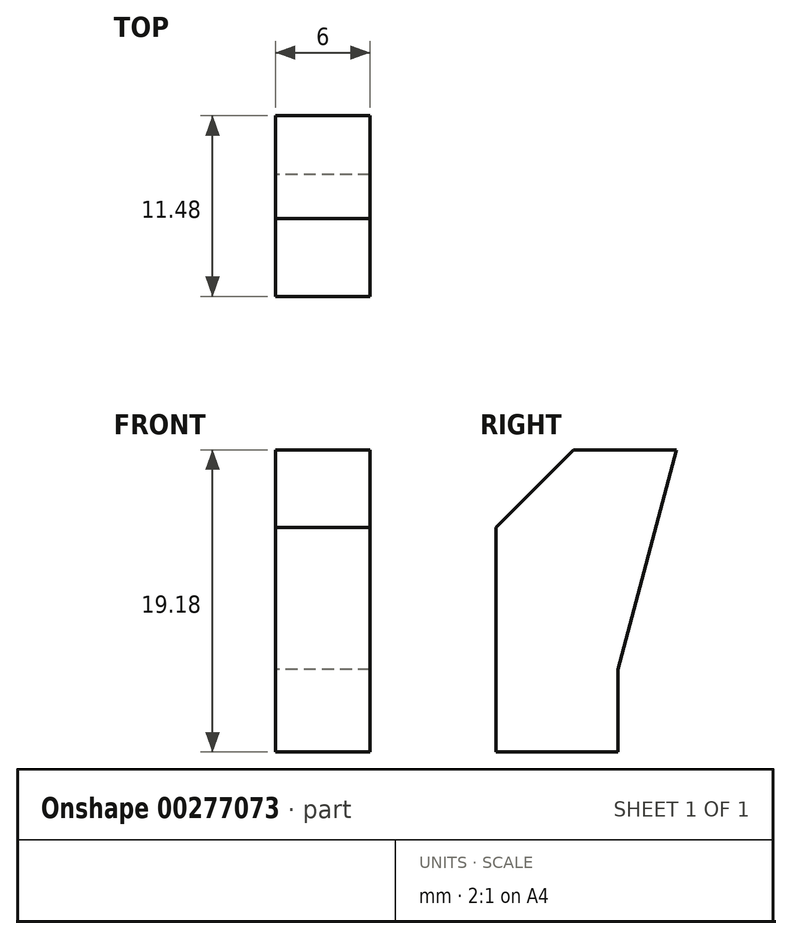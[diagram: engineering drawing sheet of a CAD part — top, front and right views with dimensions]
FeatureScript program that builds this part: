
annotation { "Feature Type Name" : "Feature", "Feature Type Description" : "" }
export const myFeature = defineFeature(function(context is Context, id is Id, definition is map)
    precondition{}
    {
        {
            var Q0;
            Q0=qCreatedBy(makeId("Right.planeOp"),FACE);
            var sketch = newSketch(context, id + "F0", { "sketchPlane" : qUnion([Q0])});
            skLineSegment(sketch, "E0", {"start": v(0, 0) * mm, "end": v(-6.99, 0) * mm, "construction": true});
            skLineSegment(sketch, "E1", {"start": v(-6.99, 0) * mm, "end": v(-12.06, -5.08) * mm, "construction": true});
            skLineSegment(sketch, "E2", {"start": v(-12.07, -5.08) * mm, "end": v(-12.06, -19.68) * mm, "construction": true});
            skLineSegment(sketch, "E3", {"start": v(-12.07, -19.69) * mm, "end": v(-3.8, -19.69) * mm, "construction": true});
            skLineSegment(sketch, "E4", {"start": v(-3.8, -19.69) * mm, "end": v(-3.8, -14.22) * mm, "construction": true});
            skLineSegment(sketch, "E5", {"start": v(-3.8, -14.22) * mm, "end": v(0, 0) * mm, "construction": true});
            skLineSegment(sketch, "E6.0", {"start": v(-11.81, -5.19) * mm, "end": v(-11.81, -19.43) * mm});
            skLineSegment(sketch, "E6.1", {"start": v(-6.88, -0.25) * mm, "end": v(-11.81, -5.19) * mm});
            skLineSegment(sketch, "E6.2", {"start": v(0, -0.25) * mm, "end": v(-0.07, -0.25) * mm, "construction": true});
            skLineSegment(sketch, "E7.0", {"start": v(-4.06, -14.19) * mm, "end": v(-0.33, -0.25) * mm});
            skLineSegment(sketch, "E7.1", {"start": v(-11.81, -19.43) * mm, "end": v(-4.06, -19.43) * mm});
            skLineSegment(sketch, "E8.0", {"start": v(-4.06, -19.43) * mm, "end": v(-4.06, -14.19) * mm});
            skLineSegment(sketch, "E9.trimOffspring", {"start": v(-0.33, -0.25) * mm, "end": v(-6.88, -0.25) * mm});
            skSolve(sketch);
        }
        {
            var Q0;
            Q0 = qSketchRegion(id + "F0", true);
            extrude(context, id + "F1", {"entities" : qUnion([Q0]), "endBound" : BoundingType.SYMMETRIC, "depth" : (6.2 - 2 * (.1)) * mm, "offsetDistance" : 25.4 * mm});
        }
        {
            var Q0;
            Q0=makeQuery(id+"F1.opExtrude","SWEPT_FACE",FACE,{"disambiguationData":[OSD([sQuery(id+"F0.wireOp",EDGE,"E6.0")])]});
            var sketch = newSketch(context, id + "F2", { "sketchPlane" : qUnion([Q0])});
            skLineSegment(sketch, "E10.bottom", {"start": v(-78.49, -19.43) * mm, "end": v(-70.87, -19.43) * mm});
            skLineSegment(sketch, "E10.top", {"start": v(-78.49, -13.46) * mm, "end": v(-70.87, -13.46) * mm});
            skLineSegment(sketch, "E10.left", {"start": v(-78.49, -19.43) * mm, "end": v(-78.49, -13.46) * mm});
            skLineSegment(sketch, "E10.right", {"start": v(-70.87, -19.43) * mm, "end": v(-70.87, -13.46) * mm});
            skLineSegment(sketch, "E11", {"start": v(0, 0) * mm, "end": v(0, -19.43) * mm, "construction": true});
            skLineSegment(sketch, "E12.MirrorCS", {"start": v(70.87, -19.43) * mm, "end": v(70.87, -13.46) * mm});
            skLineSegment(sketch, "E13.MirrorCS", {"start": v(78.49, -19.43) * mm, "end": v(70.87, -19.43) * mm});
            skLineSegment(sketch, "E14.MirrorCS", {"start": v(78.49, -19.43) * mm, "end": v(78.49, -13.46) * mm});
            skLineSegment(sketch, "E15.MirrorCS", {"start": v(78.49, -13.46) * mm, "end": v(70.87, -13.46) * mm});
            skSolve(sketch);
        }
        {
            var Q0;
            Q0 = qSketchRegion(id + "F2", true);
            extrude(context, id + "F3", {"entities" : qUnion([Q0]), "operationType" : NewBodyOperationType.REMOVE, "oppositeDirection" : true, "depth" : 3.43 * mm, "offsetDistance" : 25.4 * mm});
        }
    });
